# Revit family: HL_Вентиляционный клапан_HL905N.0
name_source: partatom
category: Instalační zařizovací předměty
revit_build: Autodesk Revit 2016 (Build: 20151007_0715(x64)
units: mm (PartAtom-declared; Revit-internal decimal feet)

## family parameters
Bod výpočtu místnosti = Ne
Kóta kulaté spojky = Použít průměr
Nadpis OmniClass = Liquid Waste Collection and Removal
Ořezat dutým tvarem při načtení = Ne
Sdílené = Ne
Typ součásti = Normální
Vždy vertikální = Ano
Založené na pracovní rovině = Ne
Číslo OmniClass = 23.70.50.21

## types (1)
- HL_Вентиляционный клапан_HL905N.0
    Cena = 0 $
    EAN = 9003076049769
    Klíčová poznámka = HL905N.0
    Komentáře k typům = Воздушный клапан для скрытого монтажа
    Model = HL905N.0
    Popis = Вентиляционный клапан
    URL = http://www.hutterer-lechner.com
    Výrobce = HL Hutterer & Lechner GmbH
    ВЕС = 0,336 kg
    ВЫСОТА МОНТАЖА = 83 - 165 mm
    МАТЕРИАЛ = PP/ABS
    Материал = Plactic - White
    ПРОИЗВОДИТЕЛЬНОСТЬ = 13 l/s
    ПРОПУСКНАЯ СПОСОБНОСТЬ = 0.0 m³/h
    РАЗМЕР = DN50/75

## geometry (parser evidence)
native form markers: Sweep x1
no freeform markers — native parametric forms only
